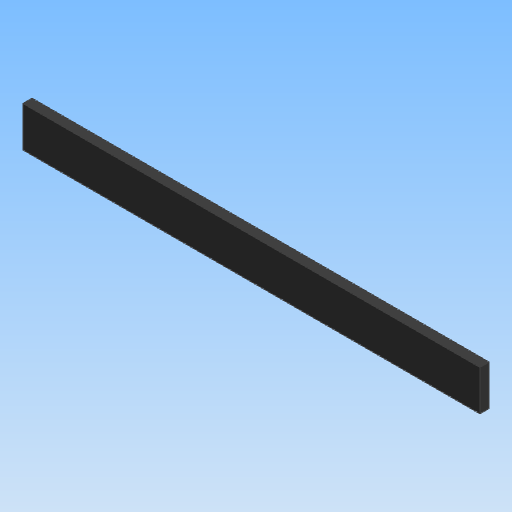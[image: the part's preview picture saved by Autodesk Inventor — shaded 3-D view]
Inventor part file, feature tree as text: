
AUTODESK INVENTOR PART (.ipt)
format: ipt  version: 2020 (Build 240168000, 168)  size: 81,920 bytes
history: native  units: mm
features: other x1, extrude x1
ambient origin geometry x8: Origin, YZ Plane, XZ Plane, XY Plane, X Axis, Y Axis, Z Axis, Center Point
bodies: Body1 (feature_tree)
feature tree (2):
  other  "實體1"
  extrude  "擠出1"  Depth=11.0mm
